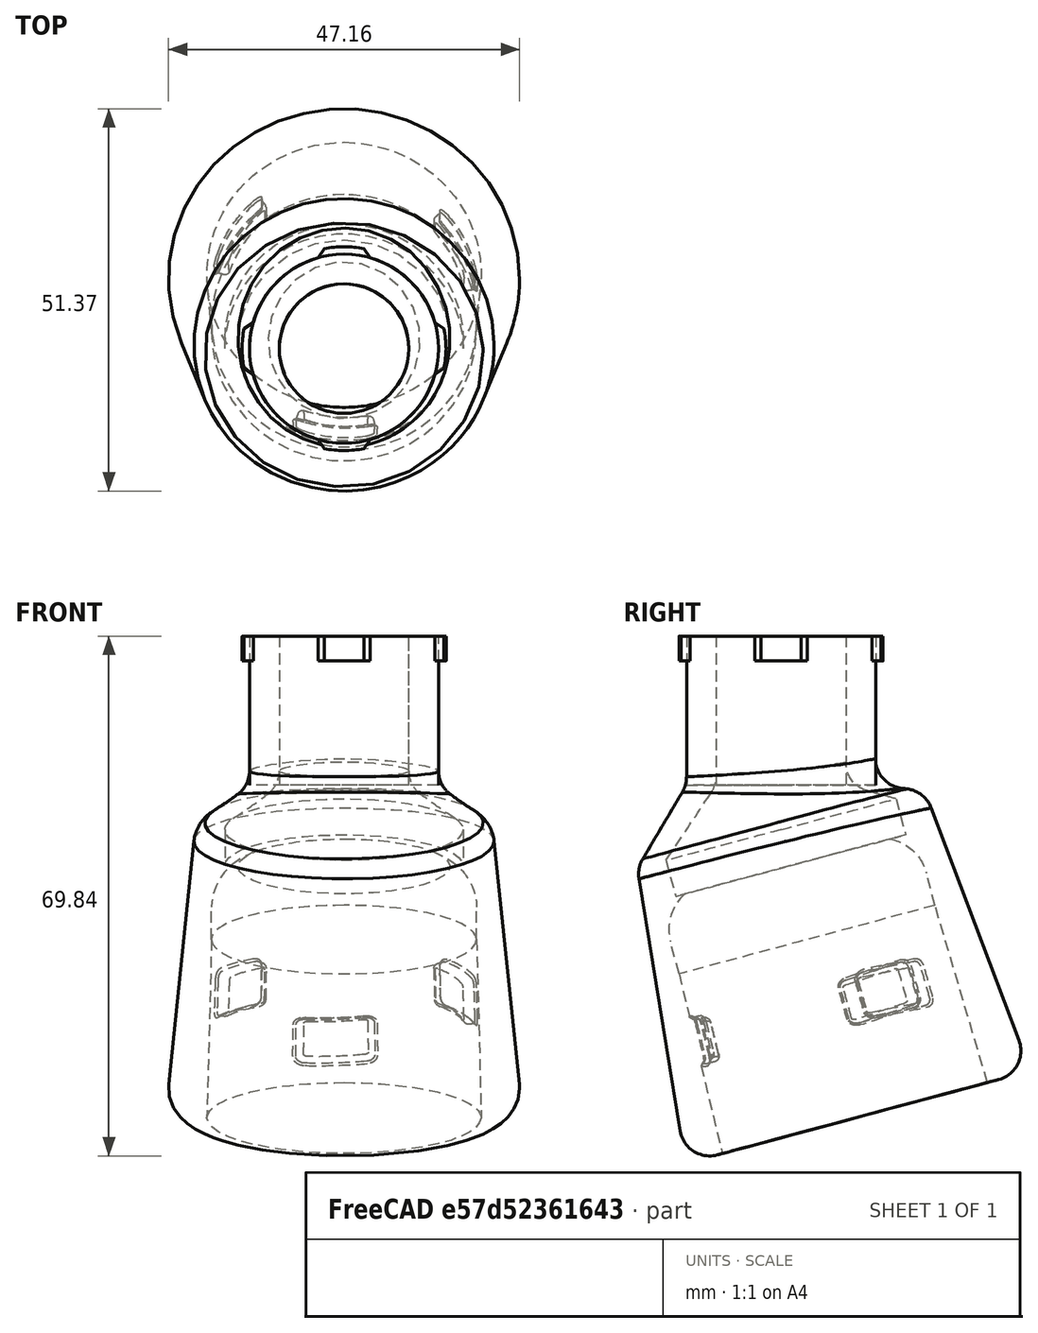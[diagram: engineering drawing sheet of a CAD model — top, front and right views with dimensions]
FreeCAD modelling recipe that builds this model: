
FCSTD DOCUMENT  (FreeCAD 0.19R)
Label: PorterCableBeltSander
License: Creative Commons Attribution-NonCommercial
LicenseURL: http://creativecommons.org/licenses/by-nc/4.0/
objects: Sketcher::SketchObject×6, Part::Cut×3, PartDesign::Pad×2, PartDesign::Body×2, Part::Feature×2, Part::Loft×2, PartDesign::PolarPattern×1, Part::Cone×1, Part::Cylinder×1, Part::Fuse×1, App::Link×1, Part::MultiFuse×1, PartDesign::FeatureBase×1, PartDesign::Fillet×1, Mesh::Feature×1
note: 27 computed .brp shape members not serialized (recipe doc carries the construction recipe); baked Part::Feature solids carry a one-line shape summary decoded from their .brp
EXTERNAL_REF file=VacuumNozzle.FCStd obj=Body001

FEATURE [Sketcher::SketchObject] Sketch
  FullyConstrained = true
  MapMode = 5
  Support = -> [XY_Plane]
  sketch-geometry (2):
    g0: Circle CenterX=0 CenterY=0 CenterZ=0 NormalX=0 NormalY=0 NormalZ=1 AngleXU=0 Radius=12.7
    g1: Circle CenterX=0 CenterY=0 CenterZ=0 NormalX=0 NormalY=0 NormalZ=1 AngleXU=0 Radius=8.7
  constraints (4):
    c: Coincident(g0,g-1)
    c: Radius(g0) = 12.7
    c: Coincident(g1,g0)
    c: Radius(g1) = 8.7
FEATURE [PartDesign::Pad] Pad
  Direction = (1,1,1)
  Length = 20
  Length2 = 100
  Profile = -> Sketch
  Type = 0
FEATURE [Sketcher::SketchObject] Sketch001
  ExternalGeometry = -> [Pad]
  FullyConstrained = true
  MapMode = 5
  Placement = pos=(0,0,20) rot=(0,0,1;0rad)
  Support = -> [Pad]
  sketch-geometry (5):
    g0: ArcOfCircle CenterX=0 CenterY=0 CenterZ=0 NormalX=0 NormalY=0 NormalZ=1 AngleXU=0 Radius=12.7 StartAngle=1.29159 EndAngle=1.85
    g1: ArcOfCircle CenterX=0 CenterY=0 CenterZ=0 NormalX=0 NormalY=0 NormalZ=1 AngleXU=0 Radius=13.7 StartAngle=1.3738 EndAngle=1.76779
    g2: LineSegment StartX=2.6814 StartY=13.435 StartZ=0 EndX=3.5 EndY=12.2082 EndZ=0
    g3: LineSegment StartX=-2.6814 StartY=13.435 StartZ=0 EndX=-3.5 EndY=12.2082 EndZ=0
    g4: LineSegment StartX=0 StartY=12.7 StartZ=0 EndX=0 EndY=13.7 EndZ=0
  constraints (16):
    c: Coincident(g1,g0)
    c: Coincident(g2,g1)
    c: Coincident(g2,g0)
    c: Coincident(g3,g1)
    c: Coincident(g3,g0)
    c: Equal(g2,g3)
    c: PointOnObject(g0,g-3)
    c: Angle(g1,g2,g1) = 2.35619
    c: Coincident(g0,g-1)
    c: Symmetric(g1,g1,g-2)
    c: Distance(g0,g0) = 7
    c: PointOnObject(g4,g0)
    c: PointOnObject(g4,g1)
    c: Perpendicular(g1,g4)
    c: Distance(g4) = 1
    c: PointOnObject(g4,g-2)
FEATURE [PartDesign::Pad] Pad001
  BaseFeature = -> Pad
  Direction = (1,1,1)
  Length = 3.34
  Length2 = 100
  Profile = -> Sketch001
  Reversed = true
  Type = 0
FEATURE [PartDesign::PolarPattern] PolarPattern
  Angle = 360
  Axis = -> Sketch001 [N_Axis]
  BaseFeature = -> Pad001
  Occurrences = 2
  Originals = -> [Pad001]
FEATURE [PartDesign::Body] Body
  Group = -> [Sketch,Pad,Sketch001,Pad001,PolarPattern]
  Origin = -> Origin
  Tip = -> PolarPattern
FEATURE [Part::Feature] PolarPattern001  label="BayonetteStub(old)"
  shape: bbox 27.4 x 25.4 x 20 mm, 14 faces (baked)
FEATURE [Part::Cone] Cone
  Angle = 360
  AttacherType = Attacher::AttachEngine3D
  AttachmentOffset = pos=(0,0,6) rot=(1,0,0;0.261799rad)
  Height = 40
  MapMode = 5
  Placement = pos=(0,0,-6) rot=(1,0,0;3.40339rad)
  Radius1 = 20
  Radius2 = 24
  Support = -> [PolarPattern001]
FEATURE [Part::Cylinder] Cylinder
  Angle = 360
  AttacherType = Attacher::AttachEngine3D
  Height = 5
  MapMode = 5
  Placement = pos=(0,0,-6) rot=(0,0.991445,0.130526;3.14159rad)
  Radius = 16
  Support = -> [Cone]
FEATURE [Part::Cut] Cut
  Base = -> Cone
  Tool = -> Cylinder
FEATURE [Sketcher::SketchObject] Sketch002
  ExternalGeometry = -> [PolarPattern001]
  FullyConstrained = false
  MapMode = 5
  Placement = pos=(0,0,0) rot=(1,0,0;3.14159rad)
  Support = -> [PolarPattern001]
  sketch-geometry (1):
    g0: Circle CenterX=0 CenterY=0 CenterZ=0 NormalX=0 NormalY=0 NormalZ=1 AngleXU=0 Radius=12.7
  constraints (1):
    c: Equal(g0,g-3)
FEATURE [Sketcher::SketchObject] Sketch003
  ExternalGeometry = -> [Cut]
  FullyConstrained = false
  MapMode = 5
  Placement = pos=(0,1.5,-5.59808) rot=(1,0,0;0.261799rad)
  Support = -> [Cut]
  sketch-geometry (1):
    g0: Circle CenterX=0 CenterY=-1.55291 CenterZ=0 NormalX=0 NormalY=0 NormalZ=1 AngleXU=0 Radius=20
  constraints (1):
    c: Equal(g0,g-3)
FEATURE [Part::Loft] Loft
  Closed = false
  MaxDegree = 5
  Ruled = false
  Sections = -> [Sketch002,Sketch003]
  Solid = true
FEATURE [Sketcher::SketchObject] Sketch004
  ExternalGeometry = -> [Sketch003]
  FullyConstrained = false
  MapMode = 5
  Placement = pos=(0,1.5,-5.59808) rot=(1,0,0;3.40339rad)
  Support = -> [Loft]
  sketch-geometry (2):
    g0: Circle CenterX=0 CenterY=1.55291 CenterZ=0 NormalX=0 NormalY=0 NormalZ=1 AngleXU=0 Radius=16
    g1: LineSegment StartX=-17.5328 StartY=11.1759 StartZ=0 EndX=-14.0262 EndY=9.25132 EndZ=0
  constraints (5):
    c: Coincident(g0,g-3)
    c: PointOnObject(g1,g-3)
    c: PointOnObject(g1,g0)
    c: Perpendicular(g0,g1)
    c: Distance(g1) = 4
FEATURE [Sketcher::SketchObject] Sketch005
  ExternalGeometry = -> [Sketch002]
  FullyConstrained = false
  MapMode = 5
  Support = -> [Loft]
  sketch-geometry (2):
    g0: Circle CenterX=0 CenterY=0 CenterZ=0 NormalX=0 NormalY=0 NormalZ=1 AngleXU=0 Radius=8.7
    g1: LineSegment StartX=-9.48851 StartY=8.44145 StartZ=0 EndX=-6.5 EndY=5.78273 EndZ=0
  constraints (5):
    c: Coincident(g0,g-1)
    c: PointOnObject(g1,g-3)
    c: PointOnObject(g1,g0)
    c: Perpendicular(g0,g1)
    c: Distance(g1) = 4
FEATURE [Part::Loft] Loft001
  Closed = false
  MaxDegree = 5
  Ruled = false
  Sections = -> [Sketch004,Sketch005]
  Solid = true
FEATURE [Part::Cut] Cut001  label="CentreLoft"
  Base = -> Loft
  Tool = -> Loft001
FEATURE [Part::Feature] Body002  label="BayonetteStub"
  shape: bbox 25.4 x 27.4 x 20 mm, 14 faces (baked)
FEATURE [Part::Fuse] Fusion  label="Lower"
  Base = -> Cut001
  Tool = -> Body002
FEATURE [App::Link] Link  label="NozzleKnockoutV2"
  LinkPlacement = pos=(1.6365e-05,26.2701,-105.77) rot=(-0.519988,-0.519988,-0.677662;1.95044rad)
  LinkedObject = -> <external VacuumNozzle.FCStd>#Body001
  Placement = pos=(1.6365e-05,26.2701,-105.77) rot=(-0.519988,-0.519988,-0.677662;1.95044rad)
FEATURE [Part::MultiFuse] Fusion001
  Refine = true
  Shapes = -> [Cut,Fusion]
FEATURE [Part::Cut] Cut002
  Base = -> Fusion001
  Tool = -> Link
FEATURE [PartDesign::FeatureBase] BaseFeature
  BaseFeature = -> Cut002
FEATURE [PartDesign::Fillet] Fillet
  Base = -> BaseFeature [Edge3,Edge5,Edge1,Edge161]
  BaseFeature = -> BaseFeature
  Radius = 4
  SupportTransform = false
FEATURE [PartDesign::Body] Body003  label="AdapterRefine"
  BaseFeature = -> Cut002
  Group = -> [BaseFeature,Fillet]
  Origin = -> Origin001
  Tip = -> Fillet
FEATURE [Mesh::Feature] Mesh  label="AdapterRefine (Meshed)"
